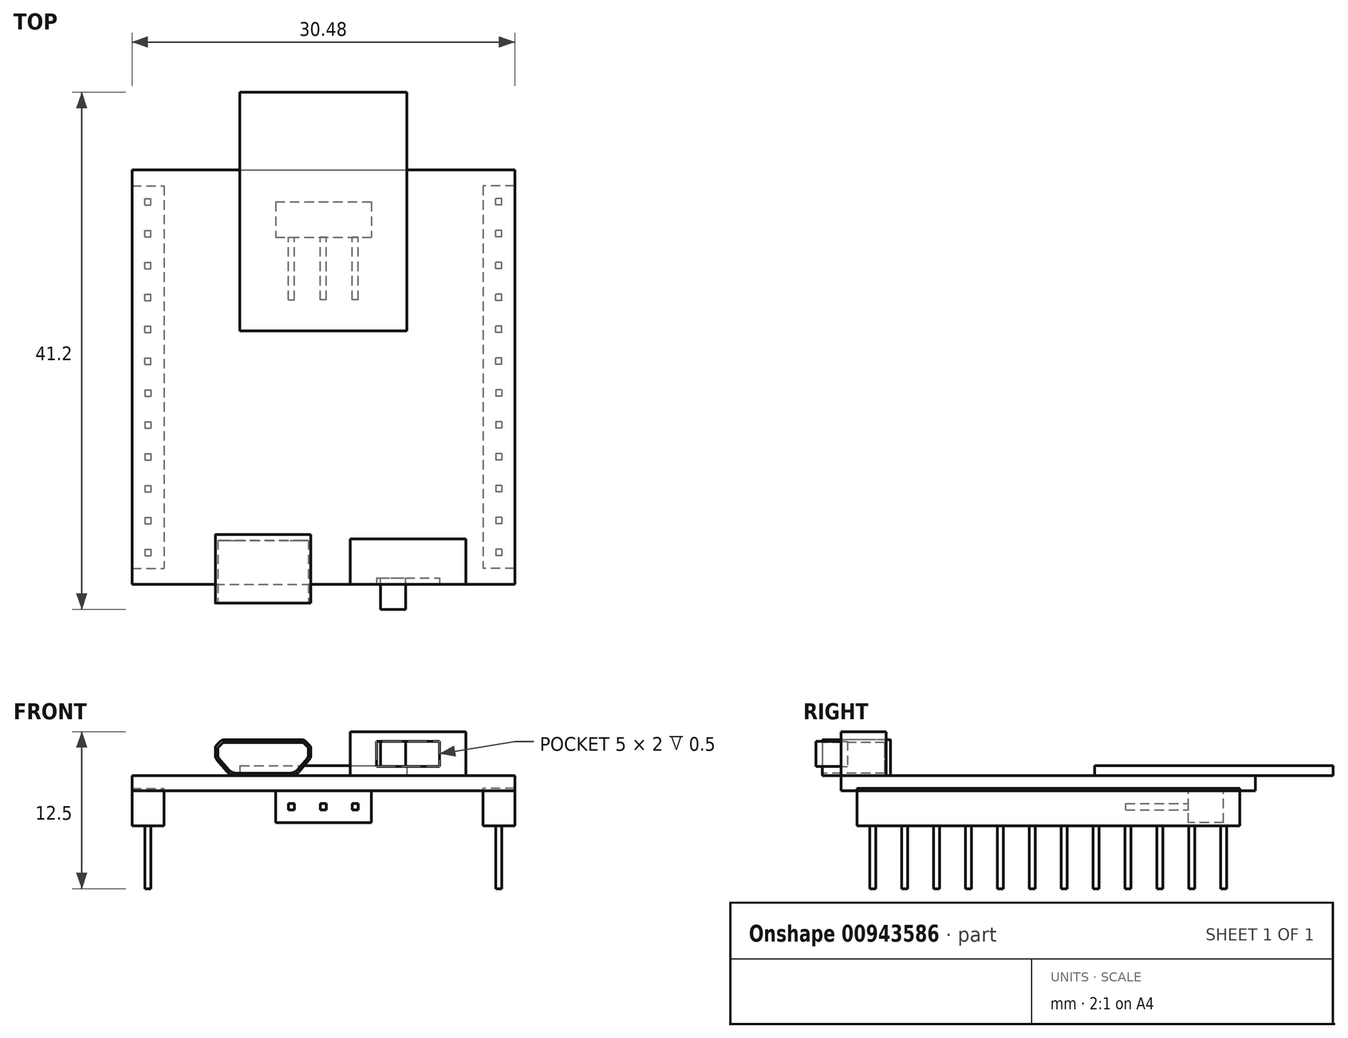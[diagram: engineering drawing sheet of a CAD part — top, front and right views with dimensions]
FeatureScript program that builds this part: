
annotation { "Feature Type Name" : "Feature", "Feature Type Description" : "" }
export const myFeature = defineFeature(function(context is Context, id is Id, definition is map)
    precondition{}
    {
        {
            var Q0;
            Q0=qCreatedBy(makeId("Top.planeOp"),FACE);
            var sketch = newSketch(context, id + "F0", { "sketchPlane" : qUnion([Q0])});
            skCircle(sketch, "E0", {"center": v(0, 0) * mm, "radius": 23 * mm, "construction": true});
            skCircle(sketch, "E1", {"center": v(0, 0) * mm, "radius": 25 * mm, "construction": true});
            skLineSegment(sketch, "E2.bottom", {"start": v(-15.24, 16) * mm, "end": v(15.24, 16) * mm});
            skLineSegment(sketch, "E2.top", {"start": v(-15.24, -17) * mm, "end": v(15.24, -17) * mm});
            skLineSegment(sketch, "E2.left", {"start": v(-15.24, 16) * mm, "end": v(-15.24, -17) * mm});
            skLineSegment(sketch, "E2.right", {"start": v(15.24, 16) * mm, "end": v(15.24, -17) * mm});
            skSolve(sketch);
        }
        {
            var Q0;
            Q0=makeQuery(id+"F0.imprint","IMPRINT",FACE,{"disambiguationData":[TD([[makeQuery(id+"F0.imprint","IMPRINT",EDGE,{"derivedFrom":sQuery(id+"F0.wireOp",EDGE,"E2.bottom")}),-1.0]])]});
            extrude(context, id + "F1", {"entities" : qUnion([Q0]), "depth" : 1.2 * mm, "offsetDistance" : 25 * mm});
        }
        {
            var Q0;
            Q0=makeQuery(id+"F1.opExtrude","CAP_FACE",FACE,{"disambiguationData":[OSD([sQuery(id+"F0.wireOp",EDGE,"E2.bottom"),sQuery(id+"F0.wireOp",EDGE,"E2.top"),sQuery(id+"F0.wireOp",EDGE,"E2.left"),sQuery(id+"F0.wireOp",EDGE,"E2.right")])],"isStart":false});
            var sketch = newSketch(context, id + "F2", { "sketchPlane" : qUnion([Q0])});
            skLineSegment(sketch, "E3.bottom", {"start": v(-6.65, 22.2) * mm, "end": v(6.65, 22.2) * mm});
            skLineSegment(sketch, "E3.top", {"start": v(-6.65, 3.2) * mm, "end": v(6.65, 3.2) * mm});
            skLineSegment(sketch, "E3.left", {"start": v(-6.65, 22.2) * mm, "end": v(-6.65, 3.2) * mm});
            skLineSegment(sketch, "E3.right", {"start": v(6.65, 22.2) * mm, "end": v(6.65, 3.2) * mm});
            skSolve(sketch);
        }
        {
            var Q0;
            Q0 = qSketchRegion(id + "F2", true);
            extrude(context, id + "F3", {"entities" : qUnion([Q0]), "depth" : 0.8 * mm, "offsetDistance" : 25 * mm});
        }
        {
            var Q0;
            Q0=makeQuery(id+"F1.opExtrude","CAP_FACE",FACE,{"disambiguationData":[OSD([sQuery(id+"F0.wireOp",EDGE,"E2.bottom"),sQuery(id+"F0.wireOp",EDGE,"E2.top"),sQuery(id+"F0.wireOp",EDGE,"E2.left"),sQuery(id+"F0.wireOp",EDGE,"E2.right")])],"isStart":false});
            var sketch = newSketch(context, id + "F4", { "sketchPlane" : qUnion([Q0])});
            skLineSegment(sketch, "E4.bottom", {"start": v(-8.6, -13.05) * mm, "end": v(-1, -13.05) * mm});
            skLineSegment(sketch, "E4.top", {"start": v(-8.6, -18.5) * mm, "end": v(-1, -18.5) * mm});
            skLineSegment(sketch, "E4.left", {"start": v(-8.6, -13.05) * mm, "end": v(-8.6, -18.5) * mm});
            skLineSegment(sketch, "E4.right", {"start": v(-1, -13.05) * mm, "end": v(-1, -18.5) * mm});
            skSolve(sketch);
        }
        {
            var Q0;
            Q0 = qSketchRegion(id + "F4", true);
            extrude(context, id + "F5", {"entities" : qUnion([Q0]), "depth" : 2.85 * mm, "offsetDistance" : 25 * mm});
        }
        {
            var Q0;
            Q0=makeQuery(id+"F5.opExtrude","SWEPT_FACE",FACE,{"disambiguationData":[OSD([sQuery(id+"F4.wireOp",EDGE,"E4.top")])]});
            var sketch = newSketch(context, id + "F6", { "sketchPlane" : qUnion([Q0])});
            skLineSegment(sketch, "E5", {"start": v(-4.8, 4.05) * mm, "end": v(-7.95, 4.05) * mm});
            skLineSegment(sketch, "E6", {"start": v(-8.16, 3.96) * mm, "end": v(-8.51, 3.61) * mm});
            skLineSegment(sketch, "E7", {"start": v(-8.6, 3.4) * mm, "end": v(-8.6, 2.8) * mm});
            skLineSegment(sketch, "E8", {"start": v(-8.48, 2.49) * mm, "end": v(-7.7, 1.56) * mm});
            skPoint(sketch, "E9.visualSharp", {"position": v(-8.08, 4.05) * mm});
            skArc(sketch, "E9.filletArc", {"start": v(-7.95, 4.05) * mm, "mid": v(-8.07, 4.03) * mm, "end": v(-8.16, 3.96) * mm});
            skPoint(sketch, "E10.visualSharp", {"position": v(-8.6, 3.52) * mm});
            skArc(sketch, "E10.filletArc", {"start": v(-8.51, 3.61) * mm, "mid": v(-8.58, 3.52) * mm, "end": v(-8.6, 3.4) * mm});
            skPoint(sketch, "E11.visualSharp", {"position": v(-8.6, 2.62) * mm});
            skArc(sketch, "E11.filletArc", {"start": v(-8.6, 2.8) * mm, "mid": v(-8.57, 2.64) * mm, "end": v(-8.48, 2.49) * mm});
            skPoint(sketch, "E12.visualSharp", {"position": v(-7.4, 1.2) * mm});
            skArc(sketch, "E12.filletArc", {"start": v(-7.7, 1.56) * mm, "mid": v(-7.36, 1.3) * mm, "end": v(-6.94, 1.2) * mm});
            skLineSegment(sketch, "E13.bottom", {"start": v(-16.54, 8.25) * mm, "end": v(11.11, 8.25) * mm});
            skLineSegment(sketch, "E13.top", {"start": v(-16.54, 1.2) * mm, "end": v(-6.94, 1.2) * mm});
            skLineSegment(sketch, "E13.left", {"start": v(-16.54, 8.25) * mm, "end": v(-16.54, 1.2) * mm});
            skLineSegment(sketch, "E13.right", {"start": v(11.11, 8.25) * mm, "end": v(11.11, 1.2) * mm});
            skLineSegment(sketch, "E14.trimOffspring", {"start": v(6.94, 1.2) * mm, "end": v(11.11, 1.2) * mm});
            skPoint(sketch, "E15.end.orphan", {"position": v(-4.8, 1.2) * mm});
            skLineSegment(sketch, "E16", {"start": v(-4.8, 4.05) * mm, "end": v(-4.8, 5.6) * mm, "construction": true});
            skLineSegment(sketch, "E17.MirrorCS", {"start": v(-1.44, 3.96) * mm, "end": v(-1.09, 3.61) * mm});
            skArc(sketch, "E18.MirrorCS", {"start": v(-1, 2.8) * mm, "mid": v(-1.03, 2.64) * mm, "end": v(-1.12, 2.49) * mm});
            skArc(sketch, "E19.MirrorCS", {"start": v(-1.09, 3.61) * mm, "mid": v(-1.02, 3.52) * mm, "end": v(-1, 3.4) * mm});
            skArc(sketch, "E20.MirrorCS", {"start": v(-1.65, 4.05) * mm, "mid": v(-1.53, 4.03) * mm, "end": v(-1.44, 3.96) * mm});
            skLineSegment(sketch, "E21.MirrorCS", {"start": v(-1, 3.4) * mm, "end": v(-1, 2.8) * mm});
            skArc(sketch, "E22.MirrorCS", {"start": v(-1.9, 1.56) * mm, "mid": v(-2.24, 1.3) * mm, "end": v(-2.66, 1.2) * mm});
            skPoint(sketch, "E23.MirrorP", {"position": v(-2.2, 1.2) * mm});
            skPoint(sketch, "E24.MirrorP", {"position": v(-1, 3.52) * mm});
            skLineSegment(sketch, "E25.MirrorCS", {"start": v(-1.12, 2.49) * mm, "end": v(-1.9, 1.56) * mm});
            skPoint(sketch, "E26.MirrorP", {"position": v(-1.53, 4.05) * mm});
            skLineSegment(sketch, "E27.MirrorCS", {"start": v(6.94, 1.2) * mm, "end": v(-2.66, 1.2) * mm});
            skPoint(sketch, "E28.MirrorP", {"position": v(-1, 2.62) * mm});
            skLineSegment(sketch, "E29.MirrorCS", {"start": v(-4.8, 4.05) * mm, "end": v(-1.65, 4.05) * mm});
            skSolve(sketch);
        }
        {
            var Q0;
            Q0 = qSketchRegion(id + "F6", true);
            extrude(context, id + "F7", {"entities" : qUnion([Q0]), "operationType" : NewBodyOperationType.REMOVE, "oppositeDirection" : true, "depth" : 10 * mm, "offsetDistance" : 25 * mm});
        }
        {
            var Q0;
            Q0=makeQuery(id+"F1.opExtrude","CAP_FACE",FACE,{"disambiguationData":[OSD([sQuery(id+"F0.wireOp",EDGE,"E2.bottom"),sQuery(id+"F0.wireOp",EDGE,"E2.top"),sQuery(id+"F0.wireOp",EDGE,"E2.left"),sQuery(id+"F0.wireOp",EDGE,"E2.right")])],"isStart":false});
            var sketch = newSketch(context, id + "F8", { "sketchPlane" : qUnion([Q0])});
            skLineSegment(sketch, "E30.bottom", {"start": v(15.24, 14.74) * mm, "end": v(12.7, 14.74) * mm});
            skLineSegment(sketch, "E30.top", {"start": v(15.24, -15.74) * mm, "end": v(12.7, -15.74) * mm});
            skLineSegment(sketch, "E30.left", {"start": v(15.24, 14.74) * mm, "end": v(15.24, -15.74) * mm});
            skLineSegment(sketch, "E30.right", {"start": v(12.7, 14.74) * mm, "end": v(12.7, -15.74) * mm});
            skLineSegment(sketch, "E31.MirrorCS", {"start": v(-15.24, 14.74) * mm, "end": v(-15.24, -15.74) * mm});
            skLineSegment(sketch, "E32.MirrorCS", {"start": v(-12.7, 14.74) * mm, "end": v(-12.7, -15.74) * mm});
            skLineSegment(sketch, "E33.MirrorCS", {"start": v(-15.24, 14.74) * mm, "end": v(-12.7, 14.74) * mm});
            skLineSegment(sketch, "E34.MirrorCS", {"start": v(-15.24, -15.74) * mm, "end": v(-12.7, -15.74) * mm});
            skSolve(sketch);
        }
        {
            var Q0;
            Q0 = qSketchRegion(id + "F8", true);
            extrude(context, id + "F9", {"entities" : qUnion([Q0]), "oppositeDirection" : true, "depth" : 4 * mm, "offsetDistance" : 25 * mm, "hasSecondDirection" : true, "secondDirectionOppositeDirection" : true, "secondDirectionDepth" : 1 * mm});
        }
        {
            var Q0;
            Q0=makeQuery(id+"F1.opExtrude","CAP_FACE",FACE,{"disambiguationData":[OSD([sQuery(id+"F0.wireOp",EDGE,"E2.bottom"),sQuery(id+"F0.wireOp",EDGE,"E2.top"),sQuery(id+"F0.wireOp",EDGE,"E2.left"),sQuery(id+"F0.wireOp",EDGE,"E2.right")])],"isStart":false});
            var sketch = newSketch(context, id + "F10", { "sketchPlane" : qUnion([Q0])});
            skLineSegment(sketch, "E35.bottom", {"start": v(11.34, -13.4) * mm, "end": v(2.14, -13.4) * mm});
            skLineSegment(sketch, "E35.top", {"start": v(11.34, -17) * mm, "end": v(2.14, -17) * mm});
            skLineSegment(sketch, "E35.left", {"start": v(11.34, -13.4) * mm, "end": v(11.34, -17) * mm});
            skLineSegment(sketch, "E35.right", {"start": v(2.14, -13.4) * mm, "end": v(2.14, -17) * mm});
            skSolve(sketch);
        }
        {
            var Q0;
            Q0 = qSketchRegion(id + "F10", true);
            extrude(context, id + "F11", {"entities" : qUnion([Q0]), "depth" : 3.5 * mm, "offsetDistance" : 25 * mm});
        }
        {
            var Q0;
            Q0=makeQuery(id+"F11.opExtrude","SWEPT_FACE",FACE,{"disambiguationData":[OSD([sQuery(id+"F10.wireOp",EDGE,"E35.top")])]});
            var sketch = newSketch(context, id + "F12", { "sketchPlane" : qUnion([Q0])});
            skLineSegment(sketch, "E36.bottom", {"start": v(4.24, 3.95) * mm, "end": v(9.24, 3.95) * mm});
            skLineSegment(sketch, "E36.top", {"start": v(4.24, 1.95) * mm, "end": v(9.24, 1.95) * mm});
            skLineSegment(sketch, "E36.left", {"start": v(4.24, 3.95) * mm, "end": v(4.24, 1.95) * mm});
            skLineSegment(sketch, "E36.right", {"start": v(9.24, 3.95) * mm, "end": v(9.24, 1.95) * mm});
            skSolve(sketch);
        }
        {
            var Q0;
            Q0 = qSketchRegion(id + "F12", true);
            extrude(context, id + "F13", {"entities" : qUnion([Q0]), "operationType" : NewBodyOperationType.REMOVE, "oppositeDirection" : true, "depth" : 0.5 * mm, "offsetDistance" : 25 * mm});
        }
        {
            var Q0;
            Q0=makeQuery(id+"F13.boolean.opBoolean","COPY",FACE,{"derivedFrom":makeQuery(id+"F13.opExtrude","CAP_FACE",FACE,{"disambiguationData":[OSD([sQuery(id+"F12.wireOp",EDGE,"E36.bottom"),sQuery(id+"F12.wireOp",EDGE,"E36.top"),sQuery(id+"F12.wireOp",EDGE,"E36.left"),sQuery(id+"F12.wireOp",EDGE,"E36.right")])],"isStart":false})});
            var sketch = newSketch(context, id + "F14", { "sketchPlane" : qUnion([Q0])});
            skLineSegment(sketch, "E37.bottom", {"start": v(4.54, 3.95) * mm, "end": v(6.54, 3.95) * mm});
            skLineSegment(sketch, "E37.top", {"start": v(4.54, 1.95) * mm, "end": v(6.54, 1.95) * mm});
            skLineSegment(sketch, "E37.left", {"start": v(4.54, 3.95) * mm, "end": v(4.54, 1.95) * mm});
            skLineSegment(sketch, "E37.right", {"start": v(6.54, 3.95) * mm, "end": v(6.54, 1.95) * mm});
            skSolve(sketch);
        }
        {
            var Q0;
            Q0 = qSketchRegion(id + "F14", true);
            extrude(context, id + "F15", {"entities" : qUnion([Q0]), "depth" : 2.5 * mm, "offsetDistance" : 25 * mm});
        }
        {
            var Q0;
            Q0=makeQuery(id+"F1.opExtrude","CAP_FACE",FACE,{"disambiguationData":[OSD([sQuery(id+"F0.wireOp",EDGE,"E2.bottom"),sQuery(id+"F0.wireOp",EDGE,"E2.top"),sQuery(id+"F0.wireOp",EDGE,"E2.left"),sQuery(id+"F0.wireOp",EDGE,"E2.right")])],"isStart":true});
            var sketch = newSketch(context, id + "F16", { "sketchPlane" : qUnion([Q0])});
            skLineSegment(sketch, "E38.bottom", {"start": v(-3.81, -13.46) * mm, "end": v(3.81, -13.46) * mm});
            skLineSegment(sketch, "E38.top", {"start": v(-3.81, -10.66) * mm, "end": v(3.81, -10.66) * mm});
            skLineSegment(sketch, "E38.left", {"start": v(-3.81, -13.46) * mm, "end": v(-3.81, -10.66) * mm});
            skLineSegment(sketch, "E38.right", {"start": v(3.81, -13.46) * mm, "end": v(3.81, -10.66) * mm});
            skSolve(sketch);
        }
        {
            var Q0;
            Q0 = qSketchRegion(id + "F16", true);
            extrude(context, id + "F17", {"entities" : qUnion([Q0]), "depth" : 2.54 * mm, "offsetDistance" : 25 * mm});
        }
        {
            var Q0;
            Q0=makeQuery(id+"F17.opExtrude","SWEPT_FACE",FACE,{"disambiguationData":[OSD([sQuery(id+"F16.wireOp",EDGE,"E38.top")])]});
            var sketch = newSketch(context, id + "F18", { "sketchPlane" : qUnion([Q0])});
            skLineSegment(sketch, "E39.bottom", {"start": v(2.8, -1.52) * mm, "end": v(2.3, -1.52) * mm});
            skLineSegment(sketch, "E39.top", {"start": v(2.8, -1.02) * mm, "end": v(2.3, -1.02) * mm});
            skLineSegment(sketch, "E39.left", {"start": v(2.8, -1.52) * mm, "end": v(2.8, -1.02) * mm});
            skLineSegment(sketch, "E39.right", {"start": v(2.3, -1.52) * mm, "end": v(2.3, -1.02) * mm});
            skLineSegment(sketch, "E40.bottom", {"start": v(0.25, -1.52) * mm, "end": v(-0.25, -1.52) * mm});
            skLineSegment(sketch, "E40.top", {"start": v(0.25, -1.02) * mm, "end": v(-0.25, -1.02) * mm});
            skLineSegment(sketch, "E40.left", {"start": v(0.25, -1.52) * mm, "end": v(0.25, -1.02) * mm});
            skLineSegment(sketch, "E40.right", {"start": v(-0.25, -1.52) * mm, "end": v(-0.25, -1.02) * mm});
            skLineSegment(sketch, "E41", {"start": v(4.06, -1.27) * mm, "end": v(-5.32, -1.27) * mm, "construction": true});
            skLineSegment(sketch, "E42", {"start": v(2.54, -2.92) * mm, "end": v(2.54, -0.38) * mm, "construction": true});
            skLineSegment(sketch, "E43.MirrorCS", {"start": v(-2.79, -1.52) * mm, "end": v(-2.29, -1.52) * mm});
            skLineSegment(sketch, "E44.MirrorCS", {"start": v(-2.79, -1.52) * mm, "end": v(-2.79, -1.02) * mm});
            skLineSegment(sketch, "E45.MirrorCS", {"start": v(-2.79, -1.02) * mm, "end": v(-2.29, -1.02) * mm});
            skLineSegment(sketch, "E46.MirrorCS", {"start": v(-2.29, -1.52) * mm, "end": v(-2.29, -1.02) * mm});
            skSolve(sketch);
        }
        {
            var Q0;
            Q0 = qSketchRegion(id + "F18", true);
            extrude(context, id + "F19", {"entities" : qUnion([Q0]), "depth" : 5 * mm, "offsetDistance" : 25 * mm});
        }
        {
            var Q0;
            Q0=makeQuery(id+"F9.opExtrude","CAP_FACE",FACE,{"disambiguationData":[OSD([sQuery(id+"F8.wireOp",EDGE,"E30.bottom"),sQuery(id+"F8.wireOp",EDGE,"E30.top"),sQuery(id+"F8.wireOp",EDGE,"E30.left"),sQuery(id+"F8.wireOp",EDGE,"E30.right")])],"isStart":false});
            var sketch = newSketch(context, id + "F20", { "sketchPlane" : qUnion([Q0])});
            skLineSegment(sketch, "E47.bottom", {"start": v(14.22, -13.22) * mm, "end": v(13.72, -13.22) * mm});
            skLineSegment(sketch, "E47.top", {"start": v(14.22, -13.72) * mm, "end": v(13.72, -13.72) * mm});
            skLineSegment(sketch, "E47.left", {"start": v(14.22, -13.22) * mm, "end": v(14.22, -13.72) * mm});
            skLineSegment(sketch, "E47.right", {"start": v(13.72, -13.22) * mm, "end": v(13.72, -13.72) * mm});
            skLineSegment(sketch, "E48.bottom", {"start": v(14.22, -10.68) * mm, "end": v(13.72, -10.68) * mm});
            skLineSegment(sketch, "E48.top", {"start": v(14.22, -11.18) * mm, "end": v(13.72, -11.18) * mm});
            skLineSegment(sketch, "E48.left", {"start": v(14.22, -10.68) * mm, "end": v(14.22, -11.18) * mm});
            skLineSegment(sketch, "E48.right", {"start": v(13.72, -10.68) * mm, "end": v(13.72, -11.18) * mm});
            skLineSegment(sketch, "E49.bottom", {"start": v(14.22, -8.14) * mm, "end": v(13.72, -8.14) * mm});
            skLineSegment(sketch, "E49.top", {"start": v(14.22, -8.64) * mm, "end": v(13.72, -8.64) * mm});
            skLineSegment(sketch, "E49.left", {"start": v(14.22, -8.14) * mm, "end": v(14.22, -8.64) * mm});
            skLineSegment(sketch, "E49.right", {"start": v(13.72, -8.14) * mm, "end": v(13.72, -8.64) * mm});
            skLineSegment(sketch, "E50.bottom", {"start": v(14.22, -5.6) * mm, "end": v(13.72, -5.6) * mm});
            skLineSegment(sketch, "E50.top", {"start": v(14.22, -6.1) * mm, "end": v(13.72, -6.1) * mm});
            skLineSegment(sketch, "E50.left", {"start": v(14.22, -5.6) * mm, "end": v(14.22, -6.1) * mm});
            skLineSegment(sketch, "E50.right", {"start": v(13.72, -5.6) * mm, "end": v(13.72, -6.1) * mm});
            skLineSegment(sketch, "E51.bottom", {"start": v(14.22, -3.06) * mm, "end": v(13.72, -3.06) * mm});
            skLineSegment(sketch, "E51.top", {"start": v(14.22, -3.56) * mm, "end": v(13.72, -3.56) * mm});
            skLineSegment(sketch, "E51.left", {"start": v(14.22, -3.06) * mm, "end": v(14.22, -3.56) * mm});
            skLineSegment(sketch, "E51.right", {"start": v(13.72, -3.06) * mm, "end": v(13.72, -3.56) * mm});
            skLineSegment(sketch, "E52.bottom", {"start": v(14.22, -0.52) * mm, "end": v(13.72, -0.52) * mm});
            skLineSegment(sketch, "E52.top", {"start": v(14.22, -1.02) * mm, "end": v(13.72, -1.02) * mm});
            skLineSegment(sketch, "E52.left", {"start": v(14.22, -0.52) * mm, "end": v(14.22, -1.02) * mm});
            skLineSegment(sketch, "E52.right", {"start": v(13.72, -0.52) * mm, "end": v(13.72, -1.02) * mm});
            skLineSegment(sketch, "E53", {"start": v(13.97, 1.6) * mm, "end": v(13.97, -4.36) * mm, "construction": true});
            skLineSegment(sketch, "E54", {"start": v(10.65, -0.77) * mm, "end": v(10.65, -0.77) * mm});
            skPoint(sketch, "E54.startSnap0", {"position": v(14.22, -0.77) * mm});
            skLineSegment(sketch, "E55", {"start": v(10.73, -3.31) * mm, "end": v(10.73, -3.31) * mm});
            skPoint(sketch, "E55.startSnap0", {"position": v(14.22, -3.31) * mm});
            skLineSegment(sketch, "E56", {"start": v(10.73, -5.85) * mm, "end": v(10.73, -5.85) * mm});
            skPoint(sketch, "E56.startSnap0", {"position": v(14.22, -5.85) * mm});
            skLineSegment(sketch, "E57", {"start": v(10.71, -8.4) * mm, "end": v(10.71, -8.4) * mm});
            skPoint(sketch, "E57.startSnap0", {"position": v(14.22, -8.4) * mm});
            skLineSegment(sketch, "E58", {"start": v(10.77, -10.93) * mm, "end": v(10.77, -10.93) * mm});
            skPoint(sketch, "E58.startSnap0", {"position": v(14.22, -10.93) * mm});
            skLineSegment(sketch, "E59", {"start": v(10.74, -13.47) * mm, "end": v(10.74, -13.47) * mm});
            skPoint(sketch, "E59.startSnap0", {"position": v(14.22, -13.47) * mm});
            skLineSegment(sketch, "E60.0.6.0", {"start": v(14.22, -16.26) * mm, "end": v(13.72, -16.26) * mm, "construction": true});
            skLineSegment(sketch, "E60.0.6.1", {"start": v(14.22, -15.76) * mm, "end": v(14.22, -16.26) * mm, "construction": true});
            skLineSegment(sketch, "E60.0.6.2", {"start": v(14.22, -15.76) * mm, "end": v(13.72, -15.76) * mm, "construction": true});
            skLineSegment(sketch, "E60.0.6.3", {"start": v(13.72, -15.76) * mm, "end": v(13.72, -16.26) * mm, "construction": true});
            skLineSegment(sketch, "E60.direction1", {"start": v(13.72, -1.02) * mm, "end": v(18.9, -1.02) * mm, "construction": true});
            skLineSegment(sketch, "E60.direction2", {"start": v(13.72, -1.02) * mm, "end": v(13.72, -3.56) * mm, "construction": true});
            skLineSegment(sketch, "E61.MirrorCS", {"start": v(-14.22, -5.6) * mm, "end": v(-14.22, -6.1) * mm});
            skLineSegment(sketch, "E62.MirrorCS", {"start": v(-14.22, -1.02) * mm, "end": v(-13.72, -1.02) * mm});
            skLineSegment(sketch, "E63.MirrorCS", {"start": v(-14.22, -13.22) * mm, "end": v(-14.22, -13.72) * mm});
            skLineSegment(sketch, "E64.MirrorCS", {"start": v(-14.22, -13.72) * mm, "end": v(-13.72, -13.72) * mm});
            skLineSegment(sketch, "E65.MirrorCS", {"start": v(-14.22, -13.22) * mm, "end": v(-13.72, -13.22) * mm});
            skLineSegment(sketch, "E66.MirrorCS", {"start": v(-13.72, -13.22) * mm, "end": v(-13.72, -13.72) * mm});
            skLineSegment(sketch, "E67.MirrorCS", {"start": v(-14.22, -8.64) * mm, "end": v(-13.72, -8.64) * mm});
            skLineSegment(sketch, "E68.MirrorCS", {"start": v(-14.22, -6.1) * mm, "end": v(-13.72, -6.1) * mm});
            skLineSegment(sketch, "E69.MirrorCS", {"start": v(-14.22, -5.6) * mm, "end": v(-13.72, -5.6) * mm});
            skLineSegment(sketch, "E70.MirrorCS", {"start": v(-14.22, -10.68) * mm, "end": v(-13.72, -10.68) * mm});
            skLineSegment(sketch, "E71.MirrorCS", {"start": v(-13.72, -10.68) * mm, "end": v(-13.72, -11.18) * mm});
            skLineSegment(sketch, "E72.MirrorCS", {"start": v(-14.22, -8.14) * mm, "end": v(-14.22, -8.64) * mm});
            skLineSegment(sketch, "E73.MirrorCS", {"start": v(-14.22, -3.56) * mm, "end": v(-13.72, -3.56) * mm});
            skLineSegment(sketch, "E74.MirrorCS", {"start": v(-14.22, -15.76) * mm, "end": v(-14.22, -16.26) * mm, "construction": true});
            skLineSegment(sketch, "E75.MirrorCS", {"start": v(-14.22, -3.06) * mm, "end": v(-14.22, -3.56) * mm});
            skLineSegment(sketch, "E76.MirrorCS", {"start": v(-14.22, -10.68) * mm, "end": v(-14.22, -11.18) * mm});
            skLineSegment(sketch, "E77.MirrorCS", {"start": v(-14.22, -11.18) * mm, "end": v(-13.72, -11.18) * mm});
            skLineSegment(sketch, "E78.MirrorCS", {"start": v(-14.22, -0.52) * mm, "end": v(-13.72, -0.52) * mm});
            skLineSegment(sketch, "E79.MirrorCS", {"start": v(-13.72, -3.06) * mm, "end": v(-13.72, -3.56) * mm});
            skLineSegment(sketch, "E80.MirrorCS", {"start": v(-14.22, -3.06) * mm, "end": v(-13.72, -3.06) * mm});
            skLineSegment(sketch, "E81.MirrorCS", {"start": v(-14.22, -15.76) * mm, "end": v(-13.72, -15.76) * mm, "construction": true});
            skLineSegment(sketch, "E82.MirrorCS", {"start": v(-13.72, -5.6) * mm, "end": v(-13.72, -6.1) * mm});
            skLineSegment(sketch, "E83.MirrorCS", {"start": v(-13.72, -8.14) * mm, "end": v(-13.72, -8.64) * mm});
            skLineSegment(sketch, "E84.MirrorCS", {"start": v(-14.22, -8.14) * mm, "end": v(-13.72, -8.14) * mm});
            skLineSegment(sketch, "E85.MirrorCS", {"start": v(-14.22, -0.52) * mm, "end": v(-14.22, -1.02) * mm});
            skLineSegment(sketch, "E86.MirrorCS", {"start": v(-14.22, -16.26) * mm, "end": v(-13.72, -16.26) * mm, "construction": true});
            skLineSegment(sketch, "E87.MirrorCS", {"start": v(-13.72, -15.76) * mm, "end": v(-13.72, -16.26) * mm, "construction": true});
            skLineSegment(sketch, "E88.MirrorCS", {"start": v(-13.72, -0.52) * mm, "end": v(-13.72, -1.02) * mm});
            skPoint(sketch, "E89.MirrorP", {"position": v(-14.22, -3.31) * mm});
            skPoint(sketch, "E90.MirrorP", {"position": v(-14.22, -0.77) * mm});
            skPoint(sketch, "E91.MirrorP", {"position": v(-14.22, -5.85) * mm});
            skPoint(sketch, "E92.MirrorP", {"position": v(-14.22, -13.47) * mm});
            skPoint(sketch, "E93.MirrorP", {"position": v(-14.22, -10.93) * mm});
            skPoint(sketch, "E94.MirrorP", {"position": v(-14.22, -8.4) * mm});
            skLineSegment(sketch, "E95", {"start": v(3.38, 0.5) * mm, "end": v(8.13, 0.5) * mm, "construction": true});
            skLineSegment(sketch, "E96.MirrorCS", {"start": v(-13.72, 4.06) * mm, "end": v(-13.72, 4.56) * mm});
            skLineSegment(sketch, "E97.MirrorCS", {"start": v(-14.22, 14.22) * mm, "end": v(-14.22, 14.72) * mm});
            skLineSegment(sketch, "E98.MirrorCS", {"start": v(-13.72, 6.6) * mm, "end": v(-13.72, 7.1) * mm});
            skLineSegment(sketch, "E99.MirrorCS", {"start": v(-14.22, 11.68) * mm, "end": v(-13.72, 11.68) * mm});
            skLineSegment(sketch, "E100.MirrorCS", {"start": v(-14.22, 9.64) * mm, "end": v(-13.72, 9.64) * mm});
            skLineSegment(sketch, "E101.MirrorCS", {"start": v(-14.22, 6.6) * mm, "end": v(-14.22, 7.1) * mm});
            skLineSegment(sketch, "E102.MirrorCS", {"start": v(-14.22, 7.1) * mm, "end": v(-13.72, 7.1) * mm});
            skLineSegment(sketch, "E103.MirrorCS", {"start": v(-14.22, 11.68) * mm, "end": v(-14.22, 12.18) * mm});
            skLineSegment(sketch, "E104.MirrorCS", {"start": v(-14.22, 4.06) * mm, "end": v(-14.22, 4.56) * mm});
            skLineSegment(sketch, "E105.MirrorCS", {"start": v(-13.72, 11.68) * mm, "end": v(-13.72, 12.18) * mm});
            skLineSegment(sketch, "E106.MirrorCS", {"start": v(-14.22, 12.18) * mm, "end": v(-13.72, 12.18) * mm});
            skLineSegment(sketch, "E107.MirrorCS", {"start": v(-14.22, 9.14) * mm, "end": v(-14.22, 9.64) * mm});
            skLineSegment(sketch, "E108.MirrorCS", {"start": v(-14.22, 4.06) * mm, "end": v(-13.72, 4.06) * mm});
            skLineSegment(sketch, "E109.MirrorCS", {"start": v(-14.22, 9.14) * mm, "end": v(-13.72, 9.14) * mm});
            skLineSegment(sketch, "E110.MirrorCS", {"start": v(-14.22, 14.22) * mm, "end": v(-13.72, 14.22) * mm});
            skLineSegment(sketch, "E111.MirrorCS", {"start": v(-14.22, 6.6) * mm, "end": v(-13.72, 6.6) * mm});
            skLineSegment(sketch, "E112.MirrorCS", {"start": v(-14.22, 4.56) * mm, "end": v(-13.72, 4.56) * mm});
            skLineSegment(sketch, "E113.MirrorCS", {"start": v(-14.22, 14.72) * mm, "end": v(-13.72, 14.72) * mm});
            skLineSegment(sketch, "E114.MirrorCS", {"start": v(-13.72, 9.14) * mm, "end": v(-13.72, 9.64) * mm});
            skLineSegment(sketch, "E115.MirrorCS", {"start": v(-13.72, 14.22) * mm, "end": v(-13.72, 14.72) * mm});
            skLineSegment(sketch, "E116.MirrorCS", {"start": v(-14.22, 2.02) * mm, "end": v(-13.72, 2.02) * mm});
            skLineSegment(sketch, "E117.MirrorCS", {"start": v(-14.22, 17.26) * mm, "end": v(-13.72, 17.26) * mm, "construction": true});
            skLineSegment(sketch, "E118.MirrorCS", {"start": v(-13.72, 16.76) * mm, "end": v(-13.72, 17.26) * mm, "construction": true});
            skLineSegment(sketch, "E119.MirrorCS", {"start": v(-13.72, 1.52) * mm, "end": v(-13.72, 2.02) * mm});
            skLineSegment(sketch, "E120.MirrorCS", {"start": v(-14.22, 16.76) * mm, "end": v(-14.22, 17.26) * mm, "construction": true});
            skLineSegment(sketch, "E121.MirrorCS", {"start": v(-14.22, 16.76) * mm, "end": v(-13.72, 16.76) * mm, "construction": true});
            skLineSegment(sketch, "E122.MirrorCS", {"start": v(-14.22, 1.52) * mm, "end": v(-14.22, 2.02) * mm});
            skLineSegment(sketch, "E123.MirrorCS", {"start": v(-14.22, 1.52) * mm, "end": v(-13.72, 1.52) * mm});
            skPoint(sketch, "E124.MirrorP", {"position": v(-14.22, 11.93) * mm});
            skPoint(sketch, "E125.MirrorP", {"position": v(-14.22, 9.39) * mm});
            skPoint(sketch, "E126.MirrorP", {"position": v(-14.22, 4.3) * mm});
            skPoint(sketch, "E127.MirrorP", {"position": v(-14.22, 1.77) * mm});
            skPoint(sketch, "E128.MirrorP", {"position": v(-14.22, 6.85) * mm});
            skPoint(sketch, "E129.MirrorP", {"position": v(-14.22, 14.47) * mm});
            skLineSegment(sketch, "E130.MirrorCS", {"start": v(14.22, 6.6) * mm, "end": v(14.22, 7.1) * mm});
            skLineSegment(sketch, "E131.MirrorCS", {"start": v(13.72, 9.14) * mm, "end": v(13.72, 9.64) * mm});
            skLineSegment(sketch, "E132.MirrorCS", {"start": v(13.72, 4.06) * mm, "end": v(13.72, 4.56) * mm});
            skLineSegment(sketch, "E133.MirrorCS", {"start": v(14.22, 14.72) * mm, "end": v(13.72, 14.72) * mm});
            skLineSegment(sketch, "E134.MirrorCS", {"start": v(14.22, 4.56) * mm, "end": v(13.72, 4.56) * mm});
            skLineSegment(sketch, "E135.MirrorCS", {"start": v(14.22, 7.1) * mm, "end": v(13.72, 7.1) * mm});
            skLineSegment(sketch, "E136.MirrorCS", {"start": v(14.22, 9.14) * mm, "end": v(13.72, 9.14) * mm});
            skLineSegment(sketch, "E137.MirrorCS", {"start": v(14.22, 4.06) * mm, "end": v(14.22, 4.56) * mm});
            skLineSegment(sketch, "E138.MirrorCS", {"start": v(14.22, 11.68) * mm, "end": v(14.22, 12.18) * mm});
            skLineSegment(sketch, "E139.MirrorCS", {"start": v(14.22, 6.6) * mm, "end": v(13.72, 6.6) * mm});
            skLineSegment(sketch, "E140.MirrorCS", {"start": v(13.72, 14.22) * mm, "end": v(13.72, 14.72) * mm});
            skLineSegment(sketch, "E141.MirrorCS", {"start": v(14.22, 4.06) * mm, "end": v(13.72, 4.06) * mm});
            skLineSegment(sketch, "E142.MirrorCS", {"start": v(14.22, 14.22) * mm, "end": v(13.72, 14.22) * mm});
            skLineSegment(sketch, "E143.MirrorCS", {"start": v(14.22, 12.18) * mm, "end": v(13.72, 12.18) * mm});
            skLineSegment(sketch, "E144.MirrorCS", {"start": v(14.22, 14.22) * mm, "end": v(14.22, 14.72) * mm});
            skLineSegment(sketch, "E145.MirrorCS", {"start": v(14.22, 9.14) * mm, "end": v(14.22, 9.64) * mm});
            skLineSegment(sketch, "E146.MirrorCS", {"start": v(14.22, 11.68) * mm, "end": v(13.72, 11.68) * mm});
            skLineSegment(sketch, "E147.MirrorCS", {"start": v(13.72, 11.68) * mm, "end": v(13.72, 12.18) * mm});
            skLineSegment(sketch, "E148.MirrorCS", {"start": v(14.22, 9.64) * mm, "end": v(13.72, 9.64) * mm});
            skLineSegment(sketch, "E149.MirrorCS", {"start": v(13.72, 6.6) * mm, "end": v(13.72, 7.1) * mm});
            skLineSegment(sketch, "E150.MirrorCS", {"start": v(13.72, 16.76) * mm, "end": v(13.72, 17.26) * mm, "construction": true});
            skLineSegment(sketch, "E151.MirrorCS", {"start": v(14.22, 1.52) * mm, "end": v(14.22, 2.02) * mm});
            skLineSegment(sketch, "E152.MirrorCS", {"start": v(14.22, 1.52) * mm, "end": v(13.72, 1.52) * mm});
            skLineSegment(sketch, "E153.MirrorCS", {"start": v(14.22, 16.76) * mm, "end": v(13.72, 16.76) * mm, "construction": true});
            skLineSegment(sketch, "E154.MirrorCS", {"start": v(13.72, 1.52) * mm, "end": v(13.72, 2.02) * mm});
            skLineSegment(sketch, "E155.MirrorCS", {"start": v(14.22, 16.76) * mm, "end": v(14.22, 17.26) * mm, "construction": true});
            skLineSegment(sketch, "E156.MirrorCS", {"start": v(14.22, 2.02) * mm, "end": v(13.72, 2.02) * mm});
            skLineSegment(sketch, "E157.MirrorCS", {"start": v(14.22, 17.26) * mm, "end": v(13.72, 17.26) * mm, "construction": true});
            skPoint(sketch, "E158.MirrorP", {"position": v(14.22, 11.93) * mm});
            skPoint(sketch, "E159.MirrorP", {"position": v(14.22, 6.85) * mm});
            skPoint(sketch, "E160.MirrorP", {"position": v(14.22, 9.39) * mm});
            skPoint(sketch, "E161.MirrorP", {"position": v(14.22, 14.47) * mm});
            skPoint(sketch, "E162.MirrorP", {"position": v(14.22, 1.77) * mm});
            skPoint(sketch, "E163.MirrorP", {"position": v(14.22, 4.3) * mm});
            skSolve(sketch);
        }
        {
            var Q0;
            Q0 = qSketchRegion(id + "F20", true);
            extrude(context, id + "F21", {"entities" : qUnion([Q0]), "depth" : 5 * mm, "offsetDistance" : 25 * mm});
        }
        {
            var Q0;
            Q0=makeQuery(id+"F5.opExtrude","SWEPT_FACE",FACE,{"disambiguationData":[OSD([sQuery(id+"F4.wireOp",EDGE,"E4.top")])]});
            var sketch = newSketch(context, id + "F22", { "sketchPlane" : qUnion([Q0])});
            skArc(sketch, "E164.0", {"start": v(-8.4, 2.8) * mm, "mid": v(-8.38, 2.7) * mm, "end": v(-8.33, 2.61) * mm});
            skLineSegment(sketch, "E164.1", {"start": v(-8.4, 3.4) * mm, "end": v(-8.4, 2.8) * mm});
            skArc(sketch, "E164.2", {"start": v(-8.37, 3.47) * mm, "mid": v(-8.4, 3.44) * mm, "end": v(-8.4, 3.4) * mm});
            skLineSegment(sketch, "E164.3", {"start": v(-8.02, 3.82) * mm, "end": v(-8.37, 3.47) * mm});
            skArc(sketch, "E164.4", {"start": v(-7.95, 3.85) * mm, "mid": v(-7.99, 3.84) * mm, "end": v(-8.02, 3.82) * mm});
            skLineSegment(sketch, "E164.5", {"start": v(-2.05, 1.69) * mm, "end": v(-1.27, 2.61) * mm});
            skArc(sketch, "E164.6", {"start": v(-2.66, 1.4) * mm, "mid": v(-2.32, 1.47) * mm, "end": v(-2.05, 1.69) * mm});
            skLineSegment(sketch, "E164.7", {"start": v(-6.94, 1.4) * mm, "end": v(-2.66, 1.4) * mm});
            skArc(sketch, "E164.8", {"start": v(-7.55, 1.69) * mm, "mid": v(-7.28, 1.47) * mm, "end": v(-6.94, 1.4) * mm});
            skArc(sketch, "E164.9", {"start": v(-1.27, 2.61) * mm, "mid": v(-1.22, 2.7) * mm, "end": v(-1.2, 2.8) * mm});
            skLineSegment(sketch, "E164.10", {"start": v(-1.2, 2.8) * mm, "end": v(-1.2, 3.4) * mm});
            skArc(sketch, "E164.11", {"start": v(-1.2, 3.4) * mm, "mid": v(-1.2, 3.44) * mm, "end": v(-1.23, 3.47) * mm});
            skLineSegment(sketch, "E164.12", {"start": v(-1.23, 3.47) * mm, "end": v(-1.58, 3.82) * mm});
            skArc(sketch, "E164.13", {"start": v(-1.58, 3.82) * mm, "mid": v(-1.61, 3.84) * mm, "end": v(-1.65, 3.85) * mm});
            skLineSegment(sketch, "E164.14", {"start": v(-8.33, 2.61) * mm, "end": v(-7.55, 1.69) * mm});
            skLineSegment(sketch, "E164.15", {"start": v(-1.65, 3.85) * mm, "end": v(-7.95, 3.85) * mm});
            skSolve(sketch);
        }
        {
            var Q0;
            Q0 = qSketchRegion(id + "F22", true);
            extrude(context, id + "F23", {"entities" : qUnion([Q0]), "operationType" : NewBodyOperationType.REMOVE, "oppositeDirection" : true, "depth" : 5 * mm, "offsetDistance" : 25 * mm});
        }
    });
